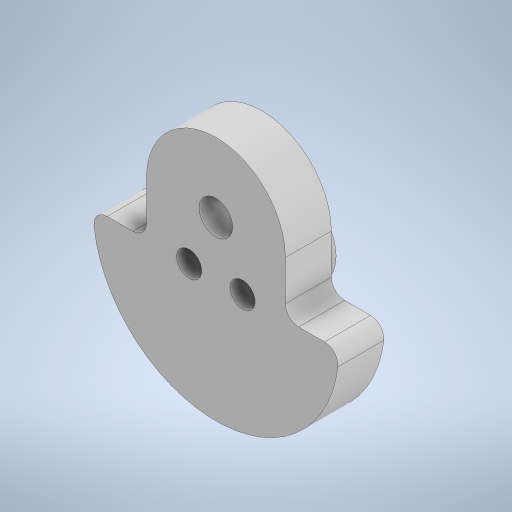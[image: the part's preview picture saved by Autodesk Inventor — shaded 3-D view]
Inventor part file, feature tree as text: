
AUTODESK INVENTOR PART (.ipt)
format: ipt  version: 2023 (Build 270158000, 158)  size: 483,328 bytes
history: native  units: in
note: dims shown in document units (in); Inventor stores cm internally (conversion verified against a paired STEP export)
features: extrude x5, sketch x1, fillet x1
ambient origin geometry x8: Origin, YZ Plane, XZ Plane, XY Plane, X Axis, Y Axis, Z Axis, Center Point
bodies: Body1 (feature_tree)
feature tree (7):
  sketch  "Sketch1"  dims[d3=0.866in d15=0.75in d20=0.314in d37=0.75in d44=0.125in d51=0.235in d52=0.235in d57=0.74in d58=0.75in d59=0.0in d60=0.32in d61=0.0in d62=1.5in d63=0.0in d64=1.5in d65=0.0in d66=0.375in d67=0.0in d68=0.125in d69=0.132in d70=0.132in]
  extrude  "Extrusion9"  Depth=0.125in
  extrude  "Extrusion10"  Depth=0.125in
  extrude  "Extrusion11"  Depth=0.125in
  extrude  "Extrusion12"  Depth=0.125in
  extrude  "Extrusion13"  Depth=0.125in
  fillet  "Fillet2"  Radius=0.74in
